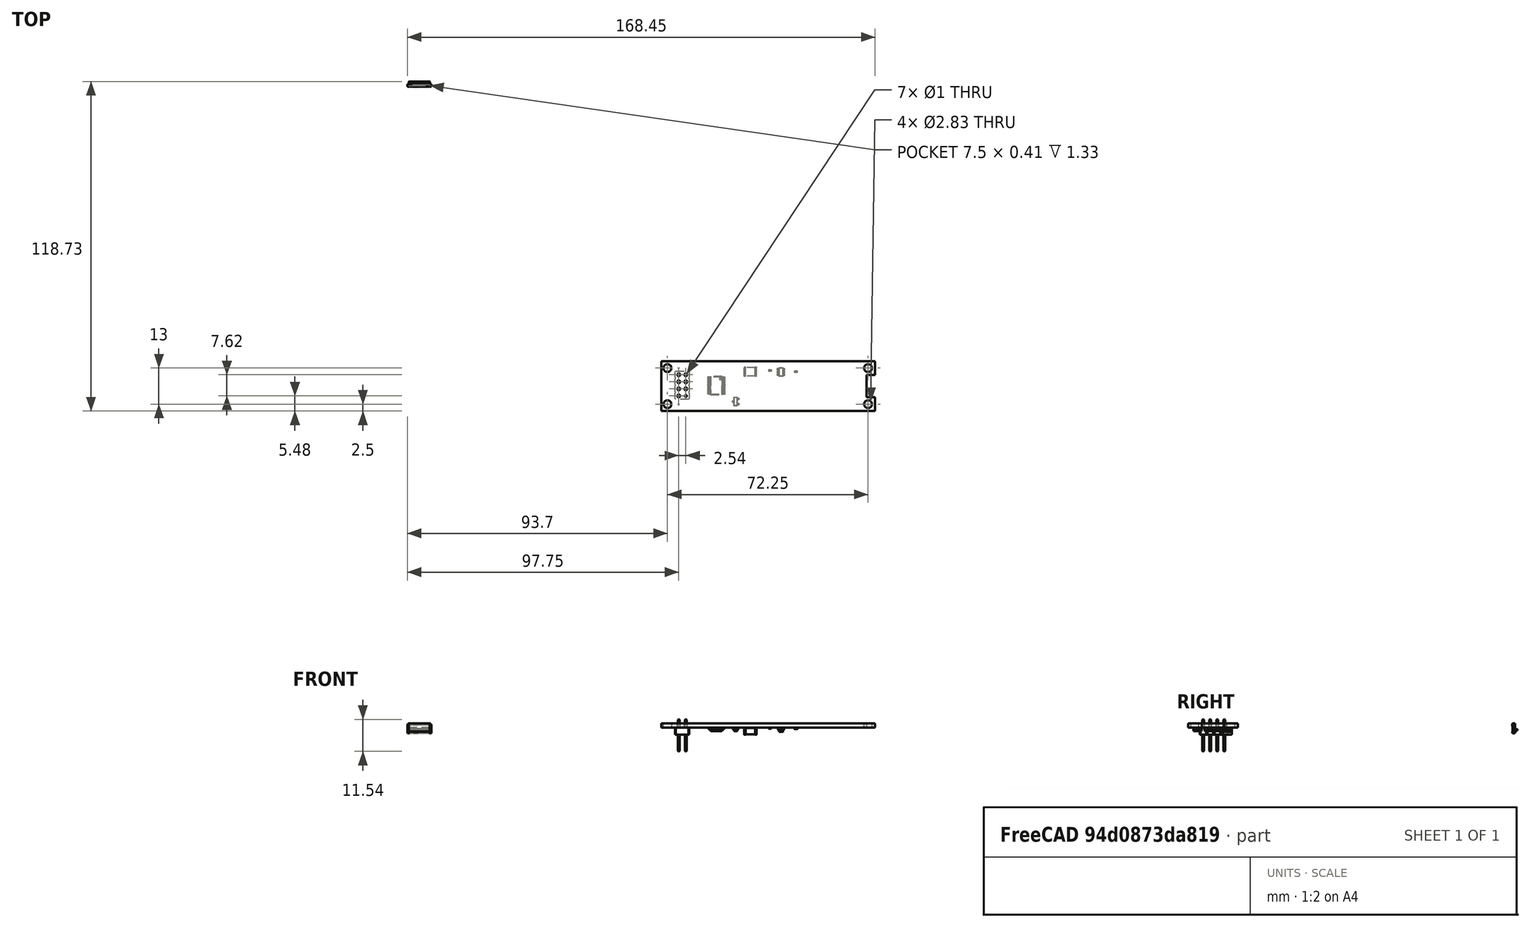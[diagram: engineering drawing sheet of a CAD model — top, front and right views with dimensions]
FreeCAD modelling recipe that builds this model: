
FCSTD DOCUMENT  (FreeCAD 0.19R24267 +148 (Git))
Label: ELW2106AA-breakout-board
License: All rights reserved
LicenseURL: http://en.wikipedia.org/wiki/All_rights_reserved
objects: Part::Feature×18, App::Link×13, App::Part×5, PartDesign::CoordinateSystem×1, Sketcher::SketchObject×1
note: 20 computed .brp shape members not serialized (recipe doc carries the construction recipe); baked Part::Feature solids carry a one-line shape summary decoded from their .brp

FEATURE [PartDesign::CoordinateSystem] Local_CS_f2d0
  AttacherType = Attacher::AttachEngine3D
FEATURE [Part::Feature] Pcb_f2d0
  Placement = pos=(0.1,0.15,0) rot=(0,0,1;0rad)
  shape: bbox 77 x 18 x 1.6 mm, 21 faces (baked)
FEATURE [Sketcher::SketchObject] PCB_Sketch_f2d0
  FullyConstrained = false
  sketch-geometry (12):
    g0: LineSegment StartX=164.1 StartY=-98.85 StartZ=0 EndX=87.1 EndY=-98.85 EndZ=0
    g1: LineSegment StartX=87.1 StartY=-116.85 StartZ=0 EndX=164.1 EndY=-116.85 EndZ=0
    g2: LineSegment StartX=164.1 StartY=-111.85 StartZ=0 EndX=164.1 EndY=-116.85 EndZ=0
    g3: LineSegment StartX=87.1 StartY=-98.85 StartZ=0 EndX=87.1 EndY=-116.85 EndZ=0
    g4: LineSegment StartX=161.1 StartY=-103.85 StartZ=0 EndX=161.1 EndY=-111.85 EndZ=0
    g5: LineSegment StartX=161.1 StartY=-111.85 StartZ=0 EndX=164.1 EndY=-111.85 EndZ=0
    g6: LineSegment StartX=164.1 StartY=-103.85 StartZ=0 EndX=161.1 EndY=-103.85 EndZ=0
    g7: LineSegment StartX=164.1 StartY=-98.85 StartZ=0 EndX=164.1 EndY=-103.85 EndZ=0
    g8: Circle CenterX=161.6 CenterY=-101.35 CenterZ=0 NormalX=0 NormalY=0 NormalZ=1 AngleXU=0 Radius=1.41421
    g9: Circle CenterX=161.6 CenterY=-114.35 CenterZ=0 NormalX=0 NormalY=0 NormalZ=1 AngleXU=0 Radius=1.41421
    g10: Circle CenterX=89.35 CenterY=-114.35 CenterZ=0 NormalX=0 NormalY=0 NormalZ=1 AngleXU=0 Radius=1.41421
    g11: Circle CenterX=89.35 CenterY=-101.35 CenterZ=0 NormalX=0 NormalY=0 NormalZ=1 AngleXU=0 Radius=1.41421
  constraints (8):
    c: Coincident(g1,g3)
    c: Coincident(g0,g3)
    c: Coincident(g4,g5)
    c: Coincident(g4,g6)
    c: Coincident(g1,g2)
    c: Coincident(g2,g5)
    c: Coincident(g6,g7)
    c: Coincident(g0,g7)
FEATURE [Part::Feature] Shape  label="U1_SOT_23_6_6b041773625d"
  Placement = pos=(130.237,-102.8,-1.6) rot=(1,0,0;3.14159rad)
  shape: bbox 2.8 x 2.9 x 1.55 mm, 124 faces (baked)
FEATURE [Part::Feature] Shape001  label="C1_C_0402_1005Metric_33167d785f6f"
  Placement = pos=(135.64,-102.7,-1.6) rot=(0,1,0;3.14159rad)
  shape: bbox 1 x 0.5 x 0.5 mm, 28 faces (baked)
FEATURE [Part::Feature] Shape002  label="L1_L_1812_4532Metric_76900049981e"
  Placement = pos=(119.237,-102.7,-1.6) rot=(0,1,0;3.14159rad)
  shape: bbox 4.5 x 3.2 x 2.5 mm, 28 faces (baked)
FEATURE [App::Link] C1_C_0402_1005Metric_33167d785f6f_ln_  label="C10_C_0402_1005Metric_f97302330d3f"
  LinkPlacement = pos=(123.55,-103.35,-1.6) rot=(0,1,0;3.14159rad)
  LinkedObject = -> Shape001
  Placement = pos=(123.55,-103.35,-1.6) rot=(0,1,0;3.14159rad)
FEATURE [App::Link] C1_C_0402_1005Metric_33167d785f6f_ln_001  label="C7_C_0402_1005Metric_00d6204cd972"
  LinkPlacement = pos=(140.1,-101.8,-1.6) rot=(0,1,0;3.14159rad)
  LinkedObject = -> Shape001
  Placement = pos=(140.1,-101.8,-1.6) rot=(0,1,0;3.14159rad)
FEATURE [Part::Feature] Shape003  label="R3_R_0402_1005Metric_60b4027e3331"
  Placement = pos=(126.25,-102.15,-1.6) rot=(1,0,0;3.14159rad)
  shape: bbox 1 x 0.5 x 0.35 mm, 26 faces (baked)
FEATURE [App::Link] R3_R_0402_1005Metric_60b4027e3331_ln_  label="R4_R_0402_1005Metric_91e1efba01da"
  LinkPlacement = pos=(126.25,-103.35,-1.6) rot=(0,1,0;3.14159rad)
  LinkedObject = -> Shape003
  Placement = pos=(126.25,-103.35,-1.6) rot=(0,1,0;3.14159rad)
FEATURE [Part::Feature] Part__Feature  label="SOLID"
  shape: bbox 8.7 x 1.896 x 3.6 mm, 594 faces (baked)
FEATURE [Part::Feature] Part__Feature001  label="COMPOUND"
  shape: bbox 8.38 x 2e-07 x 3.5 mm, 0 faces, 0 solids (baked)
FEATURE [App::Part] _03480_1400_1  label="H1_503480-1400_1_b71d17a0d4c4"
  Group = -> [Part__Feature,Part__Feature001]
  Origin = -> Origin008
  Placement = pos=(145.45,-107.75,-1.6) rot=(-0.57735,0.57735,-0.57735;2.0944rad)
FEATURE [App::Link] C1_C_0402_1005Metric_33167d785f6f_ln_002  label="C3_C_0402_1005Metric_2e73f462e199"
  LinkPlacement = pos=(135.64,-105.15,-1.6) rot=(0,1,0;3.14159rad)
  LinkedObject = -> Shape001
  Placement = pos=(135.64,-105.15,-1.6) rot=(0,1,0;3.14159rad)
FEATURE [App::Link] C1_C_0402_1005Metric_33167d785f6f_ln_003  label="C6_C_0402_1005Metric_54a2fb856132"
  LinkPlacement = pos=(137.9,-114.5,-1.6) rot=(1,0,0;3.14159rad)
  LinkedObject = -> Shape001
  Placement = pos=(137.9,-114.5,-1.6) rot=(1,0,0;3.14159rad)
FEATURE [App::Link] C1_C_0402_1005Metric_33167d785f6f_ln_004  label="C4_C_0402_1005Metric_1ff1bd5f519a"
  LinkPlacement = pos=(135.64,-100.95,-1.6) rot=(0,1,0;3.14159rad)
  LinkedObject = -> Shape001
  Placement = pos=(135.64,-100.95,-1.6) rot=(0,1,0;3.14159rad)
FEATURE [App::Link] C1_C_0402_1005Metric_33167d785f6f_ln_005  label="C13_C_0402_1005Metric_9cd951238e2d"
  LinkPlacement = pos=(101.15,-102.35,-1.6) rot=(0,1,0;3.14159rad)
  LinkedObject = -> Shape001
  Placement = pos=(101.15,-102.35,-1.6) rot=(0,1,0;3.14159rad)
FEATURE [App::Link] C1_C_0402_1005Metric_33167d785f6f_ln_006  label="C8_C_0402_1005Metric_b8d50088af35"
  LinkPlacement = pos=(134.7,-110.7,-1.6) rot=(0.707107,-0.707107,0;3.14159rad)
  LinkedObject = -> Shape001
  Placement = pos=(134.7,-110.7,-1.6) rot=(0.707107,-0.707107,0;3.14159rad)
FEATURE [App::Link] C1_C_0402_1005Metric_33167d785f6f_ln_007  label="C2_C_0402_1005Metric_af16cc843f62"
  LinkPlacement = pos=(135.64,-103.925,-1.6) rot=(0,1,0;3.14159rad)
  LinkedObject = -> Shape001
  Placement = pos=(135.64,-103.925,-1.6) rot=(0,1,0;3.14159rad)
FEATURE [App::Link] C1_C_0402_1005Metric_33167d785f6f_ln_008  label="C5_C_0402_1005Metric_94ddfc0e7be7"
  LinkPlacement = pos=(134.8,-114.45,-1.6) rot=(0,1,0;3.14159rad)
  LinkedObject = -> Shape001
  Placement = pos=(134.8,-114.45,-1.6) rot=(0,1,0;3.14159rad)
FEATURE [Part::Feature] Shape004  label="U3_TSSOP_20_44x65mm_P065mm_84bad06b87d8"
  Placement = pos=(106.95,-107.65,-1.6) rot=(0,1,0;3.14159rad)
  shape: bbox 6.4 x 6.5 x 1.2 mm, 336 faces (baked)
FEATURE [Part::Feature] Shape005  label="U2_SOT_23_9ffdd693169c"
  Placement = pos=(113.9,-113.4,-1.6) rot=(0,1,0;3.14159rad)
  shape: bbox 2.5 x 3 x 1.2 mm, 76 faces (baked)
FEATURE [App::Link] C1_C_0402_1005Metric_33167d785f6f_ln_009  label="C12_C_0402_1005Metric_a2aa6db97b72"
  LinkPlacement = pos=(112.2,-102.05,-1.6) rot=(1,0,0;3.14159rad)
  LinkedObject = -> Shape001
  Placement = pos=(112.2,-102.05,-1.6) rot=(1,0,0;3.14159rad)
FEATURE [App::Link] C1_C_0402_1005Metric_33167d785f6f_ln_010  label="C9_C_0402_1005Metric_e8d13bedf09d"
  LinkPlacement = pos=(134.8,-113,-1.6) rot=(0,1,0;3.14159rad)
  LinkedObject = -> Shape001
  Placement = pos=(134.8,-113,-1.6) rot=(0,1,0;3.14159rad)
FEATURE [Part::Feature] Shape006  label="J1_PinHeader_2x04_P254mm_Vertical_5d29a6a2ed68"
  Placement = pos=(95.94,-103.75,-1.6) rot=(0,1,0;3.14159rad)
  shape: bbox 5.08 x 10.16 x 11.54 mm, 172 faces (baked)
FEATURE [App::Link] C1_C_0402_1005Metric_33167d785f6f_ln_011  label="C11_C_0402_1005Metric_78ebdf12edf6"
  LinkPlacement = pos=(124.15,-110.7,-1.6) rot=(0.707107,0.707107,0;3.14159rad)
  LinkedObject = -> Shape001
  Placement = pos=(124.15,-110.7,-1.6) rot=(0.707107,0.707107,0;3.14159rad)
FEATURE [App::Part] Bot_f2d0
  Group = -> [Shape,Shape001,Shape002,C1_C_0402_1005Metric_33167d785f6f_ln_,C1_C_0402_1005Metric_33167d785f6f_ln_001,Shape003,R3_R_0402_1005Metric_60b4027e3331_ln_,_03480_1400_1,C1_C_0402_1005Metric_33167d785f6f_ln_002,C1_C_0402_1005Metric_33167d785f6f_ln_003,C1_C_0402_1005Metric_33167d785f6f_ln_004,C1_C_0402_1005Metric_33167d785f6f_ln_005,C1_C_0402_1005Metric_33167d785f6f_ln_006,+8 more]
  Origin = -> Origin004
FEATURE [App::Part] Step_Models_f2d0
  Group = -> [Bot_f2d0]
  Origin = -> Origin002
FEATURE [Part::Feature] botSilks_ea95
  Placement = pos=(0.1,0.15,-1.67) rot=(0,0,1;0rad)
  shape: bbox 69.17 x 16.76 x 2e-07 mm, 113 faces, 0 solids (baked)
FEATURE [Part::Feature] topSilks_e741
  Placement = pos=(0.1,0.15,0.07) rot=(0,0,1;0rad)
  shape: bbox 75.4 x 17.95 x 2e-07 mm, 5 faces, 0 solids (baked)
FEATURE [Part::Feature] pads_area001001  label="topPads_f2d0"
  Placement = pos=(0.1,0.15,0.02) rot=(0,0,1;0rad)
  shape: bbox 64.75 x 16.2 x 2e-07 mm, 19 faces, 0 solids (baked)
FEATURE [Part::Feature] tracks_area001  label="topTracks_f2d0"
  Placement = pos=(0.1,0.15,0.01) rot=(0,0,1;0rad)
  shape: bbox 41.87 x 9.55 x 2e-07 mm, 3 faces, 0 solids (baked)
FEATURE [Part::Feature] zones_area001  label="topZones_f2d0"
  Placement = pos=(0.1,0.15,0.01) rot=(0,0,1;0rad)
  shape: bbox 73.63 x 17.24 x 2e-07 mm, 1 faces, 0 solids (baked)
FEATURE [Part::Feature] pads_area001030001  label="botPads_f2d0"
  Placement = pos=(0.1,0.15,-1.62) rot=(0,0,1;0rad)
  shape: bbox 65.47 x 16.2 x 2e-07 mm, 103 faces, 0 solids (baked)
FEATURE [Part::Feature] tracks_area002001  label="botTracks_f2d0"
  Placement = pos=(0.1,0.15,-1.61) rot=(0,0,1;0rad)
  shape: bbox 63.99 x 15.05 x 2e-07 mm, 25 faces, 0 solids (baked)
FEATURE [Part::Feature] zones_area002001  label="botZones_f2d0"
  Placement = pos=(0.1,0.15,-1.61) rot=(0,0,1;0rad)
  shape: bbox 73.63 x 17.24 x 2e-07 mm, 4 faces, 0 solids (baked)
FEATURE [App::Part] Board_Geoms_f2d0
  Group = -> [Local_CS_f2d0,Pcb_f2d0,PCB_Sketch_f2d0,botSilks_ea95,topSilks_e741,pads_area001001,tracks_area001,zones_area001,pads_area001030001,tracks_area002001,zones_area002001]
  Origin = -> Origin
FEATURE [App::Part] Board_f2d0  label="ELW2106AA-breakout-board"
  Group = -> [Board_Geoms_f2d0,Step_Models_f2d0]
  Origin = -> Origin001
